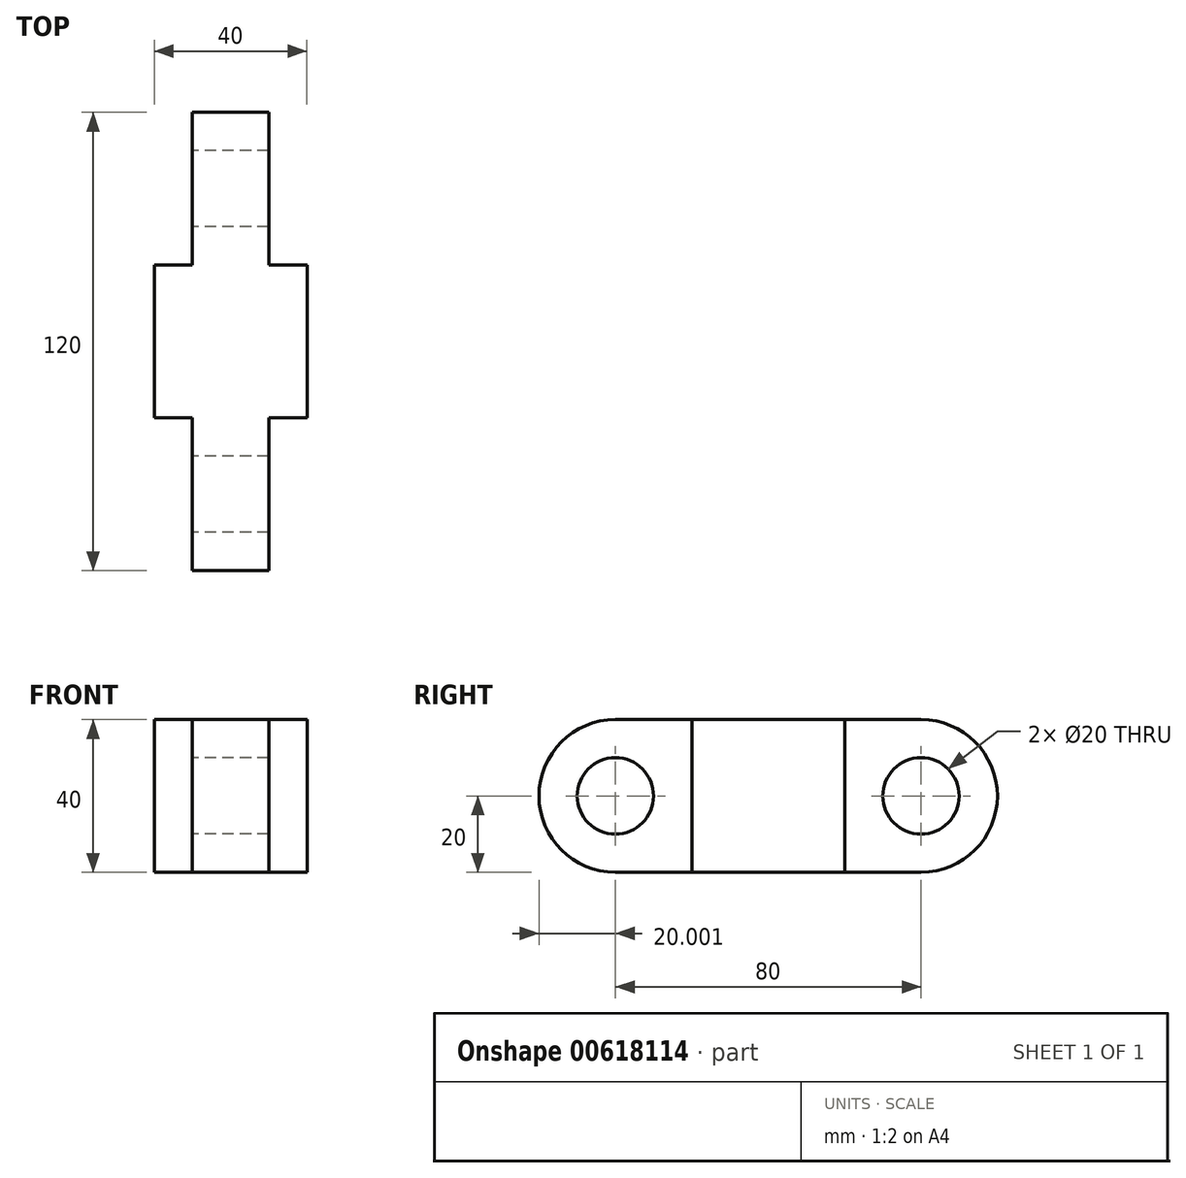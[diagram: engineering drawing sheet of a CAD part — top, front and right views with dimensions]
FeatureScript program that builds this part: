
annotation { "Feature Type Name" : "Feature", "Feature Type Description" : "" }
export const myFeature = defineFeature(function(context is Context, id is Id, definition is map)
    precondition{}
    {
        {
            var Q0;
            Q0=qCreatedBy(makeId("Top.planeOp"),FACE);
            var sketch = newSketch(context, id + "F0", { "sketchPlane" : qUnion([Q0])});
            skLineSegment(sketch, "E0", {"start": v(-20.97, 17.37) * mm, "end": v(-20.97, -22.63) * mm});
            skLineSegment(sketch, "E1", {"start": v(-10.97, -22.63) * mm, "end": v(-10.97, -62.63) * mm});
            skLineSegment(sketch, "E2", {"start": v(-10.97, -62.63) * mm, "end": v(9.03, -62.63) * mm});
            skLineSegment(sketch, "E3", {"start": v(9.03, -62.63) * mm, "end": v(9.03, -22.63) * mm});
            skLineSegment(sketch, "E4", {"start": v(9.03, -22.63) * mm, "end": v(19.03, -22.63) * mm});
            skLineSegment(sketch, "E5", {"start": v(19.03, -22.63) * mm, "end": v(19.03, 17.37) * mm});
            skLineSegment(sketch, "E6", {"start": v(19.03, 17.37) * mm, "end": v(9.03, 17.37) * mm});
            skLineSegment(sketch, "E7", {"start": v(9.03, 17.37) * mm, "end": v(9.03, 57.37) * mm});
            skLineSegment(sketch, "E8", {"start": v(9.03, 57.37) * mm, "end": v(-10.97, 57.37) * mm});
            skLineSegment(sketch, "E9", {"start": v(-10.97, 57.37) * mm, "end": v(-10.97, 17.37) * mm});
            skLineSegment(sketch, "E10", {"start": v(-10.97, 17.37) * mm, "end": v(-20.97, 17.37) * mm});
            skLineSegment(sketch, "E11", {"start": v(-20.97, -22.63) * mm, "end": v(-10.97, -22.63) * mm});
            skSolve(sketch);
        }
        {
            var Q0;
            Q0 = qSketchRegion(id + "F0", true);
            extrude(context, id + "F1", {"entities" : qUnion([Q0]), "depth" : 40 * mm, "offsetDistance" : 25 * mm});
        }
        {
            var Q0;
            Q0=makeQuery(id+"F1.opExtrude","CAP_EDGE",EDGE,{"disambiguationData":[OSD([sQuery(id+"F0.wireOp",EDGE,"E8")])],"isStart":true});
            var Q1;
            Q1=makeQuery(id+"F1.opExtrude","CAP_EDGE",EDGE,{"disambiguationData":[OSD([sQuery(id+"F0.wireOp",EDGE,"E8")])],"isStart":false});
            var Q2;
            Q2=makeQuery(id+"F1.opExtrude","CAP_EDGE",EDGE,{"disambiguationData":[OSD([sQuery(id+"F0.wireOp",EDGE,"E2")])],"isStart":false});
            var Q3;
            Q3=makeQuery(id+"F1.opExtrude","CAP_EDGE",EDGE,{"disambiguationData":[OSD([sQuery(id+"F0.wireOp",EDGE,"E2")])],"isStart":true});
            fillet(context, id + "F2", {"entities" : qUnion([Q0, Q1, Q2, Q3]), "radius" : 20 * mm, "tangentPropagation" : true, "allowEdgeOverflow" : false});
        }
        {
            var Q0;
            Q0=makeQuery(id+"F1.opExtrude","SWEPT_FACE",FACE,{"disambiguationData":[OSD([sQuery(id+"F0.wireOp",EDGE,"E9")])]});
            var sketch = newSketch(context, id + "F3", { "sketchPlane" : qUnion([Q0])});
            skCircle(sketch, "E12", {"center": v(-37.37, 20) * mm, "radius": 10 * mm});
            skSolve(sketch);
        }
        {
            var Q0;
            Q0 = qSketchRegion(id + "F3", true);
            extrude(context, id + "F4", {"entities" : qUnion([Q0]), "operationType" : NewBodyOperationType.REMOVE, "endBound" : BoundingType.UP_TO_NEXT, "oppositeDirection" : true, "depth" : 25 * mm, "offsetDistance" : 25 * mm});
        }
        {
            var Q0;
            Q0=makeQuery(id+"F1.opExtrude","SWEPT_FACE",FACE,{"disambiguationData":[OSD([sQuery(id+"F0.wireOp",EDGE,"E1")])]});
            var sketch = newSketch(context, id + "F5", { "sketchPlane" : qUnion([Q0])});
            skCircle(sketch, "E13", {"center": v(42.63, 20) * mm, "radius": 10 * mm});
            skSolve(sketch);
        }
        {
            var Q0;
            Q0 = qSketchRegion(id + "F5", true);
            extrude(context, id + "F6", {"entities" : qUnion([Q0]), "operationType" : NewBodyOperationType.REMOVE, "endBound" : BoundingType.UP_TO_NEXT, "oppositeDirection" : true, "depth" : 25 * mm, "offsetDistance" : 25 * mm});
        }
    });
